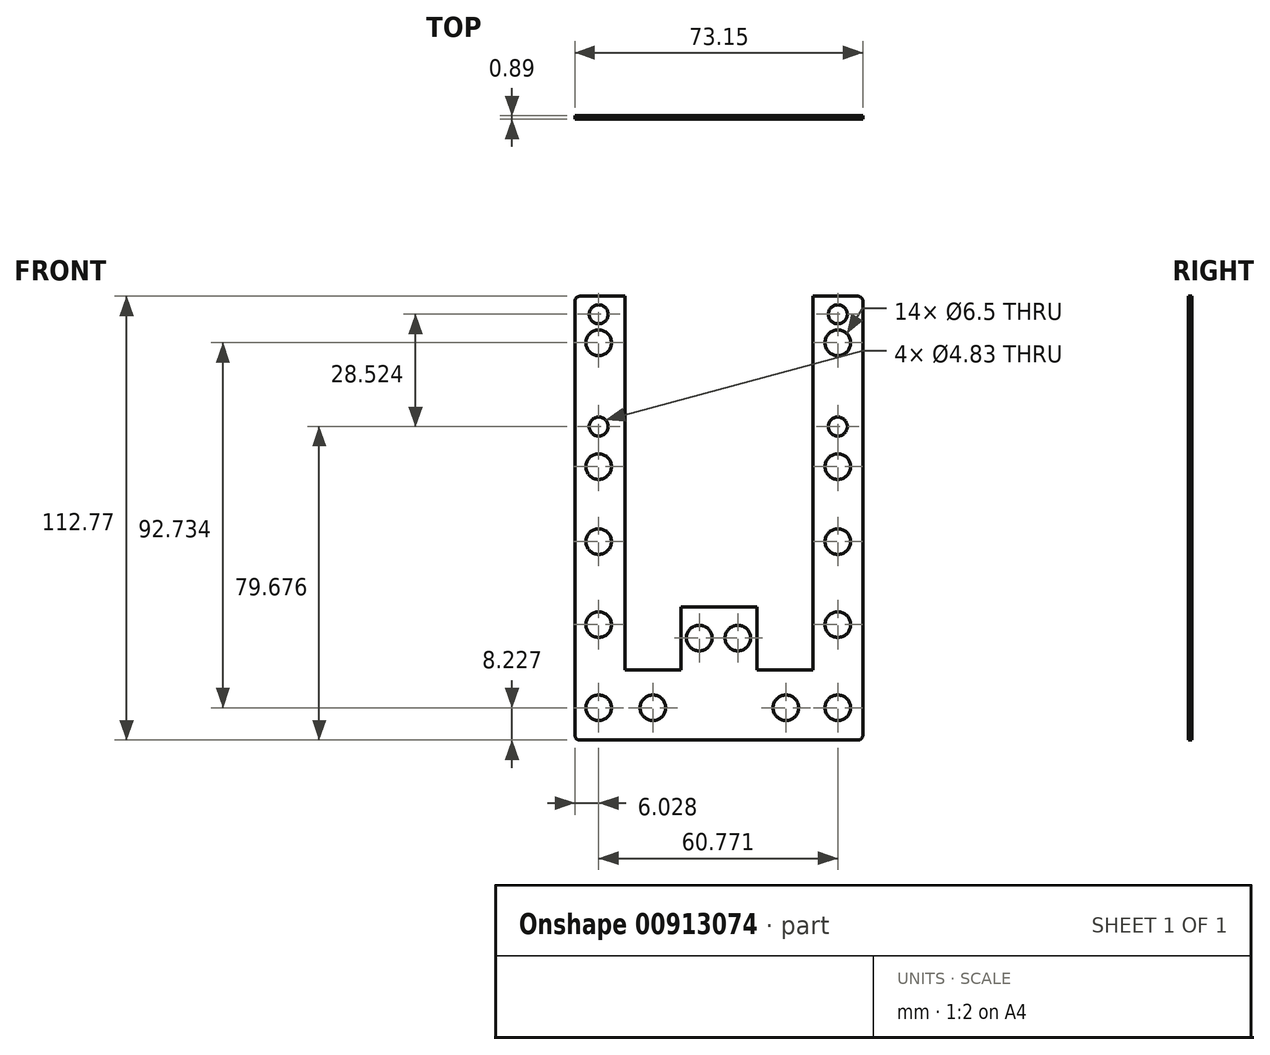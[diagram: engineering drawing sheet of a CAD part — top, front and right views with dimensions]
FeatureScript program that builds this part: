
annotation { "Feature Type Name" : "Feature", "Feature Type Description" : "" }
export const myFeature = defineFeature(function(context is Context, id is Id, definition is map)
    precondition{}
    {
        {
            var Q0;
            Q0=qCreatedBy(makeId("Front.planeOp"),FACE);
            var sketch = newSketch(context, id + "F0", { "sketchPlane" : qUnion([Q0])});
            skLineSegment(sketch, "E0", {"start": v(-36.05, 55.21) * mm, "end": v(-36.05, -55.02) * mm});
            skLineSegment(sketch, "E1", {"start": v(-34.78, -56.3) * mm, "end": v(35.83, -56.3) * mm});
            skLineSegment(sketch, "E2", {"start": v(37.1, -55.02) * mm, "end": v(37.1, 55.21) * mm});
            skLineSegment(sketch, "E3", {"start": v(35.83, 56.48) * mm, "end": v(24.4, 56.48) * mm});
            skLineSegment(sketch, "E4", {"start": v(-34.78, 56.48) * mm, "end": v(-23.35, 56.48) * mm});
            skLineSegment(sketch, "E5", {"start": v(24.4, 56.48) * mm, "end": v(24.4, -38.51) * mm});
            skLineSegment(sketch, "E6", {"start": v(-23.35, 56.48) * mm, "end": v(-23.35, -38.51) * mm});
            skLineSegment(sketch, "E7", {"start": v(-23.35, -38.51) * mm, "end": v(-9.13, -38.51) * mm});
            skLineSegment(sketch, "E8", {"start": v(24.4, -38.51) * mm, "end": v(10.17, -38.51) * mm});
            skLineSegment(sketch, "E9", {"start": v(10.17, -38.51) * mm, "end": v(10.17, -22.51) * mm});
            skLineSegment(sketch, "E10", {"start": v(-9.13, -38.51) * mm, "end": v(-9.13, -22.51) * mm});
            skLineSegment(sketch, "E11", {"start": v(-9.13, -22.51) * mm, "end": v(10.17, -22.51) * mm});
            skCircle(sketch, "E12", {"center": v(30.75, 51.91) * mm, "radius": 2.41 * mm});
            skCircle(sketch, "E13", {"center": v(-30.02, 51.91) * mm, "radius": 2.41 * mm});
            skCircle(sketch, "E14", {"center": v(30.75, 23.39) * mm, "radius": 2.41 * mm});
            skCircle(sketch, "E15", {"center": v(-30.02, 23.39) * mm, "radius": 2.41 * mm});
            skCircle(sketch, "E16", {"center": v(-30.02, 44.67) * mm, "radius": 3.25 * mm});
            skCircle(sketch, "E17", {"center": v(30.75, 44.67) * mm, "radius": 3.25 * mm});
            skCircle(sketch, "E18", {"center": v(-30.02, 13.2) * mm, "radius": 3.25 * mm});
            skCircle(sketch, "E19", {"center": v(30.75, 13.2) * mm, "radius": 3.25 * mm});
            skCircle(sketch, "E20", {"center": v(-30.02, -5.84) * mm, "radius": 3.25 * mm});
            skCircle(sketch, "E21", {"center": v(30.75, -5.84) * mm, "radius": 3.25 * mm});
            skCircle(sketch, "E22", {"center": v(-30.02, -26.95) * mm, "radius": 3.25 * mm});
            skCircle(sketch, "E23", {"center": v(30.75, -26.95) * mm, "radius": 3.25 * mm});
            skCircle(sketch, "E24", {"center": v(-30.02, -48.06) * mm, "radius": 3.25 * mm});
            skCircle(sketch, "E25", {"center": v(30.75, -48.06) * mm, "radius": 3.25 * mm});
            skCircle(sketch, "E26", {"center": v(-16.22, -48.06) * mm, "radius": 3.25 * mm});
            skCircle(sketch, "E27", {"center": v(17.56, -48.06) * mm, "radius": 3.25 * mm});
            skCircle(sketch, "E28", {"center": v(-4.47, -30.33) * mm, "radius": 3.25 * mm});
            skCircle(sketch, "E29", {"center": v(5.35, -30.33) * mm, "radius": 3.25 * mm});
            skPoint(sketch, "E30.visualSharp", {"position": v(-36.05, 56.48) * mm});
            skArc(sketch, "E30.filletArc", {"start": v(-34.78, 56.48) * mm, "mid": v(-35.68, 56.11) * mm, "end": v(-36.05, 55.21) * mm});
            skPoint(sketch, "E31.visualSharp", {"position": v(-36.05, -56.3) * mm});
            skArc(sketch, "E31.filletArc", {"start": v(-36.05, -55.02) * mm, "mid": v(-35.68, -55.92) * mm, "end": v(-34.78, -56.3) * mm});
            skPoint(sketch, "E32.visualSharp", {"position": v(37.1, -56.3) * mm});
            skArc(sketch, "E32.filletArc", {"start": v(35.83, -56.3) * mm, "mid": v(36.73, -55.92) * mm, "end": v(37.1, -55.02) * mm});
            skPoint(sketch, "E33.visualSharp", {"position": v(37.1, 56.48) * mm});
            skArc(sketch, "E33.filletArc", {"start": v(37.1, 55.21) * mm, "mid": v(36.73, 56.11) * mm, "end": v(35.83, 56.48) * mm});
            skSolve(sketch);
        }
        {
            var Q0;
            Q0=qSketchRegion(id+"F0",true);
            extrude(context, id + "F1", {"entities" : qUnion([Q0]), "depth" : 0.89 * mm, "offsetDistance" : 25.4 * mm});
        }
    });
